# Revit family: НЕВАТОМ_Вентилятор VRB, версия 1
name_source: partatom
category: Оборудование
revit_build: Autodesk Revit 2017 (Build: 20170118_1100(x64)
units: mm (PartAtom-declared; Revit-internal decimal feet)

## family parameters
Всегда вертикально = Да
На основе рабочей плоскости = Нет
Общий = Нет
При загрузке вырезать с полостями = Нет
Размер круглого соединителя = Использовать диаметр
Тип детали = Нормальный
Точка расчета площади = Нет

## types (1)
- 3.15
    A = 150 мм
    A вент = 575 мм
    A1 = 203 мм
    ADSK_Единица измерения = шт.
    ADSK_Завод-изготовитель = НЕВАТОМ
    ADSK_Количество = 1
    ADSK_Марка = Вентилятор VRB–3.15–90L–1,5/3000
    ADSK_Масса = 41
    ADSK_Масса_Текст = 41
    ADSK_Материал наименование = Сталь оцинковання
    ADSK_Наименование = Батутный вентилятор
    ADSK_Напряжение = 1500 В
    ADSK_Размер_Высота = 571 мм
    ADSK_Размер_Длина = 420 мм
    ADSK_Размер_Ширина = 575 мм
    ADSK_Ток = 0 А
    ADSK_Частота вращения вентилятора = 3000
    B = 150 мм
    B вент = 420 мм
    B1 = 221 мм
    B1+B/2 = 296 мм
    C = 214 мм
    C1 = 422 мм
    D = 315 мм
    D1 = 339 мм
    H = 571 мм
    H1 = 315 мм
    H1/5 = 63 мм
    L = 250 мм
    L-C/2 = 36 мм
    L1 = 455 мм
    Nevatom_URL = https://t.me
    Материал = <По категории>
    Материал опоры = <По категории>
    Угол = 270.00°
